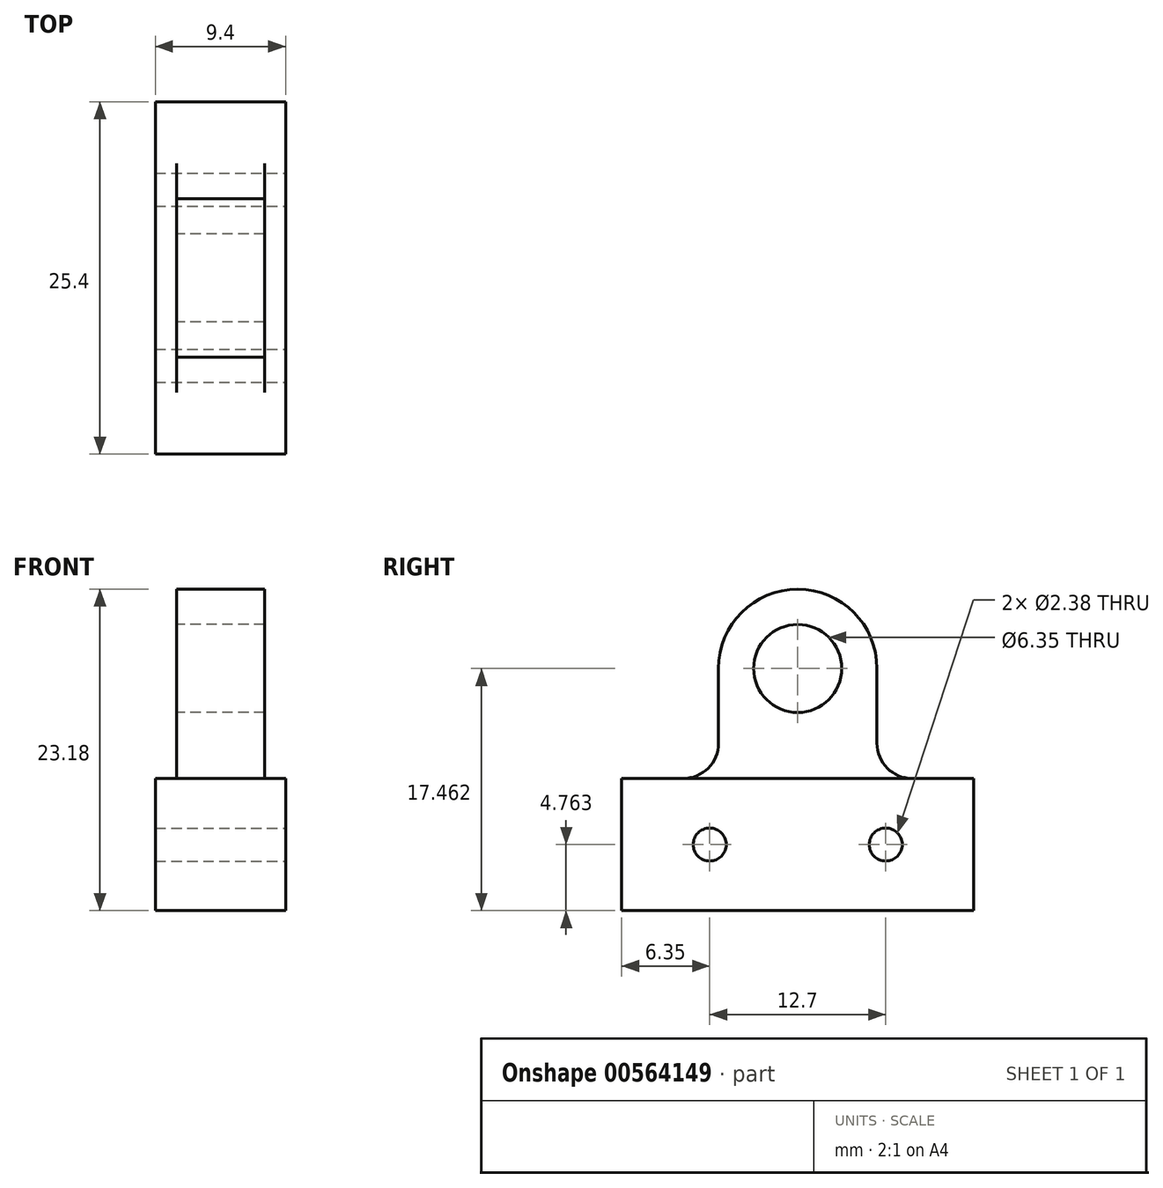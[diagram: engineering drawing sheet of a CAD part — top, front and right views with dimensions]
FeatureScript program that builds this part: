
annotation { "Feature Type Name" : "Feature", "Feature Type Description" : "" }
export const myFeature = defineFeature(function(context is Context, id is Id, definition is map)
    precondition{}
    {
        {
            var Q0;
            Q0=qCreatedBy(makeId("Right.planeOp"),FACE);
            var sketch = newSketch(context, id + "F0", { "sketchPlane" : qUnion([Q0])});
            skLineSegment(sketch, "E0.bottom", {"start": v(12.7, 0) * mm, "end": v(-12.7, 0) * mm});
            skLineSegment(sketch, "E0.top", {"start": v(12.7, 9.52) * mm, "end": v(-12.7, 9.52) * mm});
            skLineSegment(sketch, "E0.left", {"start": v(12.7, 0) * mm, "end": v(12.7, 9.53) * mm});
            skLineSegment(sketch, "E0.right", {"start": v(-12.7, 0) * mm, "end": v(-12.7, 9.52) * mm});
            skPoint(sketch, "E1", {"position": v(0, 0) * mm});
            skSolve(sketch);
        }
        {
            var Q0;
            Q0 = qSketchRegion(id + "F0", true);
            extrude(context, id + "F1", {"entities" : qUnion([Q0]), "endBound" : BoundingType.SYMMETRIC, "depth" : 9.4 * mm, "offsetDistance" : 25.4 * mm});
        }
        {
            var Q0;
            Q0=qCreatedBy(makeId("Right.planeOp"),FACE);
            var sketch = newSketch(context, id + "F2", { "sketchPlane" : qUnion([Q0])});
            skCircle(sketch, "E2", {"center": v(0, 17.46) * mm, "radius": 5.72 * mm});
            skLineSegment(sketch, "E3.bottom", {"start": v(-5.72, 17.46) * mm, "end": v(5.72, 17.46) * mm});
            skLineSegment(sketch, "E3.top", {"start": v(-5.71, 0) * mm, "end": v(5.72, 0) * mm});
            skLineSegment(sketch, "E3.left", {"start": v(-5.72, 17.46) * mm, "end": v(-5.71, 0) * mm});
            skLineSegment(sketch, "E3.right", {"start": v(5.72, 17.46) * mm, "end": v(5.72, 0) * mm});
            skCircle(sketch, "E4", {"center": v(0, 17.46) * mm, "radius": 3.18 * mm});
            skLineSegment(sketch, "E5", {"start": v(-9.92, 0) * mm, "end": v(-9.92, 9.53) * mm});
            skPoint(sketch, "E6", {"position": v(-9.92, 4.76) * mm});
            skSolve(sketch);
        }
        {
            var Q0;
            Q0 = qSketchRegion(id + "F2", true);
            extrude(context, id + "F3", {"entities" : qUnion([Q0]), "operationType" : NewBodyOperationType.ADD, "endBound" : BoundingType.SYMMETRIC, "depth" : 6.35 * mm, "offsetDistance" : 25.4 * mm});
        }
        {
            var Q0;
            Q0=makeQuery(id+"F1.opExtrude","CAP_FACE",FACE,{"disambiguationData":[OSD([sQuery(id+"F0.wireOp",EDGE,"E0.bottom"),sQuery(id+"F0.wireOp",EDGE,"E0.top"),sQuery(id+"F0.wireOp",EDGE,"E0.left"),sQuery(id+"F0.wireOp",EDGE,"E0.right")])],"isStart":false});
            var sketch = newSketch(context, id + "F4", { "sketchPlane" : qUnion([Q0])});
            skCircle(sketch, "E7", {"center": v(-6.35, 4.76) * mm, "radius": 1.2 * mm});
            skLineSegment(sketch, "E8", {"start": v(0, 0) * mm, "end": v(0, 4.09) * mm});
            skCircle(sketch, "E9.MirrorC", {"center": v(6.35, 4.76) * mm, "radius": 1.2 * mm});
            skSolve(sketch);
        }
        {
            var Q0;
            Q0 = qSketchRegion(id + "F4", true);
            extrude(context, id + "F5", {"entities" : qUnion([Q0]), "operationType" : NewBodyOperationType.REMOVE, "endBound" : BoundingType.THROUGH_ALL, "oppositeDirection" : true, "depth" : 25.4 * mm, "offsetDistance" : 25.4 * mm});
        }
        {
            var Q0;
            Q0=makeQuery(id+"F3.boolean.opBoolean","INTERSECT",EDGE,{"derivedFrom":[makeQuery(id+"F1.opExtrude","SWEPT_FACE",FACE,{"disambiguationData":[OSD([sQuery(id+"F0.wireOp",EDGE,"E0.top")])]}),makeQuery(id+"F3.opExtrude","SWEPT_FACE",FACE,{"disambiguationData":[OSD([sQuery(id+"F2.wireOp",EDGE,"E3.right")])]})]});
            var Q1;
            Q1=makeQuery(id+"F3.boolean.opBoolean","INTERSECT",EDGE,{"derivedFrom":[makeQuery(id+"F1.opExtrude","SWEPT_FACE",FACE,{"disambiguationData":[OSD([sQuery(id+"F0.wireOp",EDGE,"E0.top")])]}),makeQuery(id+"F3.opExtrude","SWEPT_FACE",FACE,{"disambiguationData":[OSD([sQuery(id+"F2.wireOp",EDGE,"E3.left")])]})]});
            fillet(context, id + "F6", {"entities" : qUnion([Q0, Q1]), "radius" : 2.54 * mm, "tangentPropagation" : true, "allowEdgeOverflow" : false});
        }
    });
